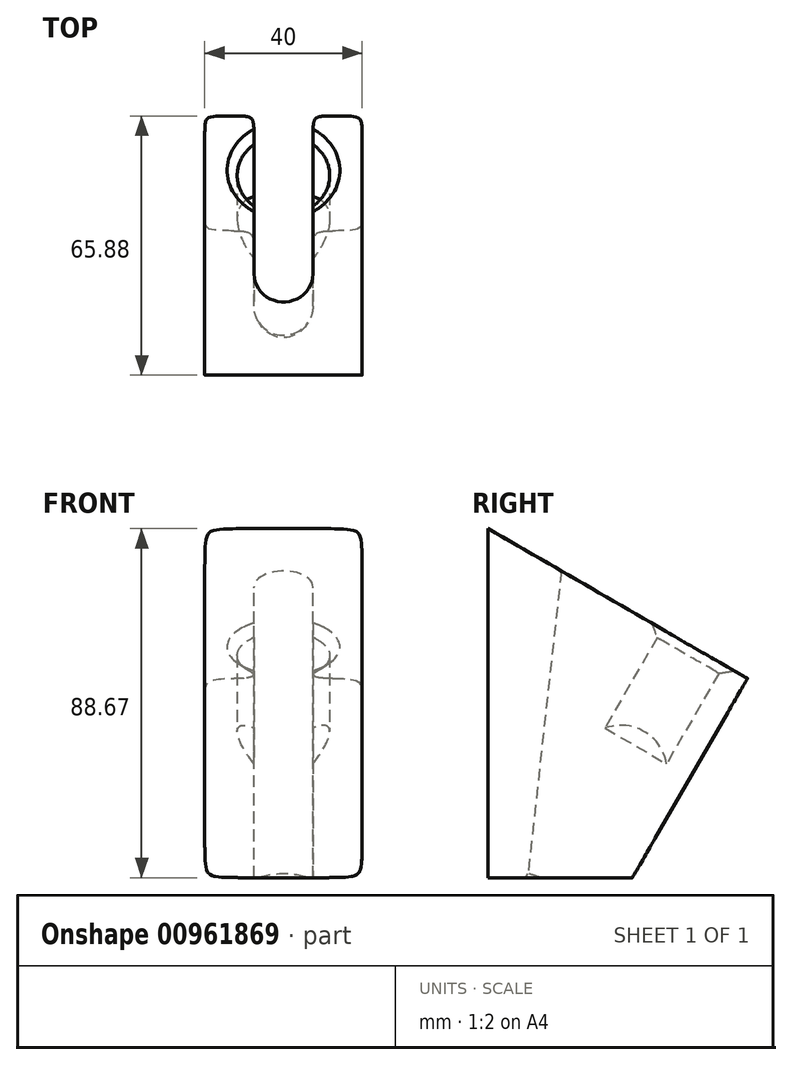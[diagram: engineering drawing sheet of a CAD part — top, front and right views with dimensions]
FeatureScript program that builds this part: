
annotation { "Feature Type Name" : "Feature", "Feature Type Description" : "" }
export const myFeature = defineFeature(function(context is Context, id is Id, definition is map)
    precondition{}
    {
        {
            var Q0;
            Q0=qCreatedBy(makeId("Right.planeOp"),FACE);
            var sketch = newSketch(context, id + "F0", { "sketchPlane" : qUnion([Q0])});
            skLineSegment(sketch, "E0", {"start": v(40, -3.13) * mm, "end": v(19.83, -38.06) * mm});
            skSolve(sketch);
        }
        {
            var Q0;
            Q0=sQuery(id+"F0.wireOp",EDGE,"E0");
            var Q1;
            Q1=sQuery(id+"F0.wireOp",VERTEX,"E0.start");
            cPlane(context, id + "F1", {"entities" : qUnion([Q0, Q1]), "cplaneType" : CPlaneType.LINE_POINT, "offset" : 25 * mm, "width" : 150 * mm, "height" : 150 * mm});
        }
        {
            var Q0;
            Q0=qCreatedBy(id+"F1.planeOp",FACE);
            var sketch = newSketch(context, id + "F2", { "sketchPlane" : qUnion([Q0])});
            skCircle(sketch, "E1", {"center": v(0, -36.2) * mm, "radius": 7.5 * mm});
            skCircle(sketch, "E2", {"center": v(0, -36.2) * mm, "radius": 11.75 * mm});
            skSolve(sketch);
        }
        {
            var Q0;
            Q0=makeQuery(id+"F2.imprint","IMPRINT",FACE,{"disambiguationData":[TD([[makeQuery(id+"F2.imprint","IMPRINT",EDGE,{"derivedFrom":sQuery(id+"F2.wireOp",EDGE,"E1")}),1.0]])]});
            extrude(context, id + "F3", {"entities" : qUnion([Q0]), "depth" : 50 * mm, "offsetDistance" : 25 * mm});
        }
        {
            var Q0;
            Q0=makeQuery(id+"F2.imprint","IMPRINT",FACE,{"disambiguationData":[TD([[makeQuery(id+"F2.imprint","IMPRINT",EDGE,{"derivedFrom":sQuery(id+"F2.wireOp",EDGE,"E1")}),-1.0]])]});
            var Q1;
            Q1=makeQuery(id+"F2.imprint","IMPRINT",FACE,{"disambiguationData":[TD([[makeQuery(id+"F2.imprint","IMPRINT",EDGE,{"derivedFrom":sQuery(id+"F2.wireOp",EDGE,"E1")}),1.0]])]});
            extrude(context, id + "F4", {"entities" : qUnion([Q0, Q1]), "operationType" : NewBodyOperationType.ADD, "oppositeDirection" : true, "depth" : 25 * mm, "offsetDistance" : 25 * mm});
        }
        {
            var Q0;
            Q0=qCreatedBy(makeId("Right.planeOp"),FACE);
            var sketch = newSketch(context, id + "F5", { "sketchPlane" : qUnion([Q0])});
            skLineSegment(sketch, "E3", {"start": v(36.66, -40.92) * mm, "end": v(65.89, 9.71) * mm});
            skLineSegment(sketch, "E4", {"start": v(65.89, 9.71) * mm, "end": v(0, 47.75) * mm});
            skLineSegment(sketch, "E5", {"start": v(36.66, -40.92) * mm, "end": v(0, -40.92) * mm});
            skLineSegment(sketch, "E6", {"start": v(0, -40.92) * mm, "end": v(0, 47.75) * mm});
            skSolve(sketch);
        }
        {
            var Q0;
            Q0=makeQuery(id+"F5.imprint","IMPRINT",FACE,{"disambiguationData":[TD([[makeQuery(id+"F5.imprint","IMPRINT",EDGE,{"derivedFrom":sQuery(id+"F5.wireOp",EDGE,"E3")}),1.0]])]});
            extrude(context, id + "F6", {"entities" : qUnion([Q0]), "endBound" : BoundingType.SYMMETRIC, "depth" : 40 * mm, "offsetDistance" : 25 * mm});
        }
        {
            var Q0;
            Q0=makeQuery(id+"F3.opExtrude","SWEPT_BODY",BODY,{"disambiguationData":[OSD([sQuery(id+"F2.wireOp",EDGE,"E1")])]});
            var Q1;
            Q1=makeQuery(id+"F6.opExtrude","SWEPT_BODY",BODY,{"disambiguationData":[OSD([sQuery(id+"F5.wireOp",EDGE,"E3"),sQuery(id+"F5.wireOp",EDGE,"E4"),sQuery(id+"F5.wireOp",EDGE,"E5"),sQuery(id+"F5.wireOp",EDGE,"E6")])]});
            booleanBodies(context, id + "F7", {"operationType" : BooleanOperationType.SUBTRACTION, "tools" : qUnion([Q0]), "targets" : qUnion([Q1])});
        }
        {
            var Q0;
            Q0=qCreatedBy(makeId("Right.planeOp"),FACE);
            var sketch = newSketch(context, id + "F8", { "sketchPlane" : qUnion([Q0])});
            skLineSegment(sketch, "E7", {"start": v(8.94, -50.74) * mm, "end": v(20.65, 55.9) * mm});
            skLineSegment(sketch, "E8", {"start": v(20.65, 55.9) * mm, "end": v(102.16, 22.97) * mm});
            skLineSegment(sketch, "E9", {"start": v(102.16, 22.97) * mm, "end": v(53.79, -51.13) * mm});
            skLineSegment(sketch, "E10", {"start": v(53.79, -51.13) * mm, "end": v(8.94, -50.74) * mm});
            skSolve(sketch);
        }
        {
            var Q0;
            Q0=makeQuery(id+"F8.imprint","IMPRINT",FACE,{"disambiguationData":[TD([[makeQuery(id+"F8.imprint","IMPRINT",EDGE,{"derivedFrom":sQuery(id+"F8.wireOp",EDGE,"E7")}),-1.0]])]});
            extrude(context, id + "F9", {"entities" : qUnion([Q0]), "operationType" : NewBodyOperationType.REMOVE, "endBound" : BoundingType.SYMMETRIC, "depth" : 15 * mm, "offsetDistance" : 25 * mm});
        }
        {
            var Q0;
            Q0=makeQuery(id+"F6.opExtrude","CAP_EDGE",EDGE,{"disambiguationData":[OSD([sQuery(id+"F5.wireOp",EDGE,"E4")])],"isStart":true});
            var Q1;
            Q1=makeQuery(id+"F6.opExtrude","CAP_EDGE",EDGE,{"disambiguationData":[OSD([sQuery(id+"F5.wireOp",EDGE,"E4")])],"isStart":false});
            var Q2;
            Q2=makeQuery(id+"F6.opExtrude","CAP_EDGE",EDGE,{"disambiguationData":[OSD([sQuery(id+"F5.wireOp",EDGE,"E5")])],"isStart":false});
            var Q3;
            Q3=makeQuery(id+"F6.opExtrude","CAP_EDGE",EDGE,{"disambiguationData":[OSD([sQuery(id+"F5.wireOp",EDGE,"E5")])],"isStart":true});
            fillet(context, id + "F10", {"entities" : qUnion([Q0, Q1, Q2, Q3]), "radius" : 10 * mm, "tangentPropagation" : true, "rho" : .8, "crossSection" : FilletCrossSection.CONIC, "allowEdgeOverflow" : false});
        }
        {
            var Q0;
            {var subQ0=sQuery(id+"F5.wireOp",EDGE,"E4");var subQ1=sQuery(id+"F2.wireOp",EDGE,"E2");Q0=makeQuery(id+"F10.opFillet","BLEND_EDGE",EDGE,{"blendedFrom":[makeQuery(id+"F6.opExtrude","CAP_EDGE",EDGE,{"disambiguationData":[OSD([subQ0])],"isStart":true}),makeQuery(id+"F9.boolean.opBoolean","SPLIT",FACE,{"disambiguationData":[TD([makeQuery(id+"F9.opExtrude","CAP_FACE",FACE,{"disambiguationData":[OSD([sQuery(id+"F8.wireOp",EDGE,"E7"),sQuery(id+"F8.wireOp",EDGE,"E8"),sQuery(id+"F8.wireOp",EDGE,"E9"),sQuery(id+"F8.wireOp",EDGE,"E10")])],"isStart":true})])],"derivedFrom":makeQuery(id+"F7.opBoolean","COPY",FACE,{"derivedFrom":makeQuery(id+"F4.opExtrude","SWEPT_FACE",FACE,{"disambiguationData":[OSD([subQ1])]})})})],"blendedInto":[makeQuery(id+"F9.boolean.opBoolean","SPLIT",FACE,{"disambiguationData":[TD([makeQuery(id+"F9.opExtrude","CAP_FACE",FACE,{"disambiguationData":[OSD([sQuery(id+"F8.wireOp",EDGE,"E7"),sQuery(id+"F8.wireOp",EDGE,"E8"),sQuery(id+"F8.wireOp",EDGE,"E9"),sQuery(id+"F8.wireOp",EDGE,"E10")])],"isStart":true})])],"derivedFrom":makeQuery(id+"F7.opBoolean","COPY",FACE,{"derivedFrom":makeQuery(id+"F4.opExtrude","SWEPT_FACE",FACE,{"disambiguationData":[OSD([subQ1])]})})})]});}
            var Q1;
            {var subQ0=makeQuery(id+"F6.opExtrude","SWEPT_FACE",FACE,{"disambiguationData":[OSD([sQuery(id+"F5.wireOp",EDGE,"E4")])]});var subQ1=makeQuery(id+"F4.opExtrude","SWEPT_FACE",FACE,{"disambiguationData":[OSD([sQuery(id+"F2.wireOp",EDGE,"E2")])]});Q1=makeQuery(id+"F9.boolean.opBoolean","SPLIT",EDGE,{"disambiguationData":[TD([makeQuery(id+"F9.opExtrude","CAP_FACE",FACE,{"disambiguationData":[OSD([sQuery(id+"F8.wireOp",EDGE,"E7"),sQuery(id+"F8.wireOp",EDGE,"E8"),sQuery(id+"F8.wireOp",EDGE,"E9"),sQuery(id+"F8.wireOp",EDGE,"E10")])],"isStart":true})])],"derivedFrom":makeQuery(id+"F7.opBoolean","INTERSECT",EDGE,{"derivedFrom":[subQ1,subQ0]})});}
            var Q2;
            {var subQ0=makeQuery(id+"F6.opExtrude","SWEPT_FACE",FACE,{"disambiguationData":[OSD([sQuery(id+"F5.wireOp",EDGE,"E4")])]});var subQ1=makeQuery(id+"F4.opExtrude","SWEPT_FACE",FACE,{"disambiguationData":[OSD([sQuery(id+"F2.wireOp",EDGE,"E2")])]});Q2=makeQuery(id+"F9.boolean.opBoolean","SPLIT",EDGE,{"disambiguationData":[TD([makeQuery(id+"F9.opExtrude","CAP_FACE",FACE,{"disambiguationData":[OSD([sQuery(id+"F8.wireOp",EDGE,"E7"),sQuery(id+"F8.wireOp",EDGE,"E8"),sQuery(id+"F8.wireOp",EDGE,"E9"),sQuery(id+"F8.wireOp",EDGE,"E10")])],"isStart":true})])],"derivedFrom":makeQuery(id+"F7.opBoolean","INTERSECT",EDGE,{"derivedFrom":[subQ1,subQ0]})});}
            var Q3;
            {var subQ0=makeQuery(id+"F6.opExtrude","SWEPT_FACE",FACE,{"disambiguationData":[OSD([sQuery(id+"F5.wireOp",EDGE,"E4")])]});var subQ1=makeQuery(id+"F4.opExtrude","SWEPT_FACE",FACE,{"disambiguationData":[OSD([sQuery(id+"F2.wireOp",EDGE,"E2")])]});Q3=makeQuery(id+"F9.boolean.opBoolean","SPLIT",EDGE,{"disambiguationData":[TD([makeQuery(id+"F9.opExtrude","CAP_FACE",FACE,{"disambiguationData":[OSD([sQuery(id+"F8.wireOp",EDGE,"E7"),sQuery(id+"F8.wireOp",EDGE,"E8"),sQuery(id+"F8.wireOp",EDGE,"E9"),sQuery(id+"F8.wireOp",EDGE,"E10")])],"isStart":false})])],"derivedFrom":makeQuery(id+"F7.opBoolean","INTERSECT",EDGE,{"derivedFrom":[subQ1,subQ0]})});}
            var Q4;
            {var subQ0=sQuery(id+"F5.wireOp",EDGE,"E4");var subQ1=sQuery(id+"F2.wireOp",EDGE,"E2");Q4=makeQuery(id+"F10.opFillet","BLEND_EDGE",EDGE,{"blendedFrom":[makeQuery(id+"F6.opExtrude","CAP_EDGE",EDGE,{"disambiguationData":[OSD([subQ0])],"isStart":false}),makeQuery(id+"F9.boolean.opBoolean","SPLIT",FACE,{"disambiguationData":[TD([makeQuery(id+"F9.opExtrude","CAP_FACE",FACE,{"disambiguationData":[OSD([sQuery(id+"F8.wireOp",EDGE,"E7"),sQuery(id+"F8.wireOp",EDGE,"E8"),sQuery(id+"F8.wireOp",EDGE,"E9"),sQuery(id+"F8.wireOp",EDGE,"E10")])],"isStart":false})])],"derivedFrom":makeQuery(id+"F7.opBoolean","COPY",FACE,{"derivedFrom":makeQuery(id+"F4.opExtrude","SWEPT_FACE",FACE,{"disambiguationData":[OSD([subQ1])]})})})],"blendedInto":[makeQuery(id+"F9.boolean.opBoolean","SPLIT",FACE,{"disambiguationData":[TD([makeQuery(id+"F9.opExtrude","CAP_FACE",FACE,{"disambiguationData":[OSD([sQuery(id+"F8.wireOp",EDGE,"E7"),sQuery(id+"F8.wireOp",EDGE,"E8"),sQuery(id+"F8.wireOp",EDGE,"E9"),sQuery(id+"F8.wireOp",EDGE,"E10")])],"isStart":false})])],"derivedFrom":makeQuery(id+"F7.opBoolean","COPY",FACE,{"derivedFrom":makeQuery(id+"F4.opExtrude","SWEPT_FACE",FACE,{"disambiguationData":[OSD([subQ1])]})})})]});}
            var Q5;
            {var subQ0=makeQuery(id+"F6.opExtrude","SWEPT_FACE",FACE,{"disambiguationData":[OSD([sQuery(id+"F5.wireOp",EDGE,"E4")])]});var subQ1=makeQuery(id+"F4.opExtrude","SWEPT_FACE",FACE,{"disambiguationData":[OSD([sQuery(id+"F2.wireOp",EDGE,"E2")])]});Q5=makeQuery(id+"F9.boolean.opBoolean","SPLIT",EDGE,{"disambiguationData":[TD([makeQuery(id+"F9.opExtrude","CAP_FACE",FACE,{"disambiguationData":[OSD([sQuery(id+"F8.wireOp",EDGE,"E7"),sQuery(id+"F8.wireOp",EDGE,"E8"),sQuery(id+"F8.wireOp",EDGE,"E9"),sQuery(id+"F8.wireOp",EDGE,"E10")])],"isStart":false})])],"derivedFrom":makeQuery(id+"F7.opBoolean","INTERSECT",EDGE,{"derivedFrom":[subQ1,subQ0]})});}
            chamfer(context, id + "F11", {"entities" : qUnion([Q0, Q1, Q2, Q3, Q4, Q5]), "width" : 2.5 * mm, "tangentPropagation" : true});
        }
        {
            var Q0;
            Q0=makeQuery(id+"F9.boolean.opBoolean","INTERSECT",EDGE,{"derivedFrom":[makeQuery(id+"F6.opExtrude","SWEPT_FACE",FACE,{"disambiguationData":[OSD([sQuery(id+"F5.wireOp",EDGE,"E3")])]}),makeQuery(id+"F9.opExtrude","CAP_FACE",FACE,{"disambiguationData":[OSD([sQuery(id+"F8.wireOp",EDGE,"E7"),sQuery(id+"F8.wireOp",EDGE,"E8"),sQuery(id+"F8.wireOp",EDGE,"E9"),sQuery(id+"F8.wireOp",EDGE,"E10")])],"isStart":false})]});
            var Q1;
            Q1=makeQuery(id+"F9.boolean.opBoolean","INTERSECT",EDGE,{"derivedFrom":[makeQuery(id+"F6.opExtrude","SWEPT_FACE",FACE,{"disambiguationData":[OSD([sQuery(id+"F5.wireOp",EDGE,"E3")])]}),makeQuery(id+"F9.opExtrude","CAP_FACE",FACE,{"disambiguationData":[OSD([sQuery(id+"F8.wireOp",EDGE,"E7"),sQuery(id+"F8.wireOp",EDGE,"E8"),sQuery(id+"F8.wireOp",EDGE,"E9"),sQuery(id+"F8.wireOp",EDGE,"E10")])],"isStart":true})]});
            fillet(context, id + "F12", {"entities" : qUnion([Q0, Q1]), "radius" : 5 * mm, "tangentPropagation" : true, "rho" : .7, "crossSection" : FilletCrossSection.CONIC, "allowEdgeOverflow" : false});
        }
        {
            var Q0;
            Q0=makeQuery(id+"F9.boolean.opBoolean","COPY",EDGE,{"derivedFrom":makeQuery(id+"F9.opExtrude","CAP_EDGE",EDGE,{"disambiguationData":[OSD([sQuery(id+"F8.wireOp",EDGE,"E7")])],"isStart":false})});
            var Q1;
            Q1=makeQuery(id+"F9.boolean.opBoolean","COPY",EDGE,{"derivedFrom":makeQuery(id+"F9.opExtrude","CAP_EDGE",EDGE,{"disambiguationData":[OSD([sQuery(id+"F8.wireOp",EDGE,"E7")])],"isStart":true})});
            fillet(context, id + "F13", {"entities" : qUnion([Q0, Q1]), "radius" : 7.5 * mm, "tangentPropagation" : true, "allowEdgeOverflow" : false});
        }
        {
            var Q0;
            Q0=makeQuery(id+"F9.boolean.opBoolean","INTERSECT",EDGE,{"derivedFrom":[makeQuery(id+"F7.opBoolean","COPY",FACE,{"derivedFrom":makeQuery(id+"F4.opExtrude","CAP_FACE",FACE,{"disambiguationData":[OSD([sQuery(id+"F2.wireOp",EDGE,"E2")])],"isStart":true})}),makeQuery(id+"F9.opExtrude","CAP_FACE",FACE,{"disambiguationData":[OSD([sQuery(id+"F8.wireOp",EDGE,"E7"),sQuery(id+"F8.wireOp",EDGE,"E8"),sQuery(id+"F8.wireOp",EDGE,"E9"),sQuery(id+"F8.wireOp",EDGE,"E10")])],"isStart":true})]});
            var Q1;
            Q1=makeQuery(id+"F9.boolean.opBoolean","INTERSECT",EDGE,{"derivedFrom":[makeQuery(id+"F7.opBoolean","COPY",FACE,{"derivedFrom":makeQuery(id+"F4.opExtrude","CAP_FACE",FACE,{"disambiguationData":[OSD([sQuery(id+"F2.wireOp",EDGE,"E2")])],"isStart":true})}),makeQuery(id+"F9.opExtrude","CAP_FACE",FACE,{"disambiguationData":[OSD([sQuery(id+"F8.wireOp",EDGE,"E7"),sQuery(id+"F8.wireOp",EDGE,"E8"),sQuery(id+"F8.wireOp",EDGE,"E9"),sQuery(id+"F8.wireOp",EDGE,"E10")])],"isStart":false})]});
            chamfer(context, id + "F14", {"entities" : qUnion([Q0, Q1]), "width" : 5 * mm, "tangentPropagation" : true});
        }
    });
